# Revit family: FP-Revit18-RS1884FRJK1-Freezer-0-CA-US-90001048A
name_source: partatom
category: Specialty Equipment
units: mm (PartAtom-declared; Revit-internal decimal feet)

## family parameters
Always vertical = Yes
Cut with Voids When Loaded = Yes
OmniClass Number = 23.40.40.11.11
OmniClass Title = Refrigerators and Freezers
Part Type = Normal
Room Calculation Point = No
Round Connector Dimension = Use Diameter
Shared = No
Work Plane-Based = No

## types (2) — shared parameters
Cavity - Depth = 635 mm
Cavity - Height = 2134 mm  [stored 7.00131 ft]
Cavity - Width = 457 mm  [stored 1.49934 ft]
Connector Description - Electrical = 120 V, 10 amp fused electrical supply
Connector Description - Water = 1/4" (6mm) comp. stainless steel braided hose
Handle Style - Contemporary Round (AHS-RD84) = No
Handle Style - Contemporary Square (AHD3-RD84) = No
Handle Style - Professional Round (AHC-RD84) = No
Handle Style - Professional Square (AHV2-RD84) = No
Manufacturer = Fisher & Paykel Appliances
Material - Body = Fisher & Paykel - Grey
Material - Door Front = Fisher & Paykel - Stainless Steel
Material - Door Structure = Fisher & Paykel - White
Material - Handle = Fisher & Paykel - Aluminium
Product - Depth (exl front panel) = 610 mm  [stored 2.00131 ft]
Product - Height = 2134 mm  [stored 7.00131 ft]
Product - Width = 451 mm  [stored 1.47966 ft]
Stainless Steel Door Panels (RD1884R4D) = No
URL = www.fisherpaykel.com
Visibility - Clearance Required = Yes
Visibility - Visibility Control Note = Yes
Visibility - Water Connection = Yes
zero-valued in all types: Default Elevation

## per-type parameters (varying)
| type | Description |
| RS1884FRJE1 | 18" Integrated Column Freezer with internal ice maker, white interior |
| RS1884FRJK1 | 18" Integrated Column Freezer with internal ice maker, stainless steel interior |

note: column(s) folded — value = type name in every type: Model

note: [stored X ft] marks values corroborated as IEEE doubles in the binary element streams (Revit-internal decimal feet)

## geometry (parser evidence)
native form markers: Sweep x12
no freeform markers — native parametric forms only
